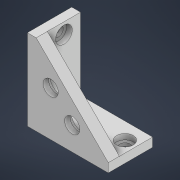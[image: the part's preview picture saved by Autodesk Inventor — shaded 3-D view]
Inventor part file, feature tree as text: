
AUTODESK INVENTOR PART (.ipt)
format: ipt  version: 2022 (Build 260153000, 153)  size: 154,112 bytes
history: native  units: mm
features: sketch x6, extrude x3, hole x3
ambient origin geometry x8: Origin, YZ Plane, XZ Plane, XY Plane, X Axis, Y Axis, Z Axis, Center Point
bodies: Volumenkörper1 (feature_tree)
feature tree (12):
  extrude  "Extrusion1"  Depth=26.0mm
  hole  "Bohrung1"  [1 undecoded]
  extrude  "Extrusion2"  Depth=13.0mm
  extrude  "Extrusion3"  Depth=9.0mm
  hole  "Bohrung2"  [1 undecoded]
  hole  "Bohrung3"  [1 undecoded]
  sketch  "Skizze1"  dims[d0=26.0mm d1=26.0mm]
  sketch  "Skizze2"  dims[d2=4.0mm d3=0.0mm]
  sketch  "Skizze3"  dims[d4=5.5mm d5=6.0mm d6=4.0mm d7=2.0mm d8=90.0deg d9=8.0mm d10=20.594885mm d11=5.5mm]
  sketch  "Skizze4"  dims[d12=5.5mm d14=13.0mm]
  sketch  "Skizze5"  dims[d15=13.0mm d16=9.0mm]
  sketch  "Skizze6"  dims[d17=9.0mm d18=2.0mm d19=0.0mm d20=3.2mm d21=3.2mm d22=16.0mm d23=0.0mm d24=3.5mm d25=6.0mm d26=6.0mm d27=2.0mm d28=90.0deg d29=8.0mm d30=20.594885mm d31=4.0mm d32=6.0mm d33=3.5mm d34=6.0mm d35=6.0mm d36=2.0mm d37=90.0deg d38=8.0mm d39=20.594885mm d40=6.0mm d41=4.0mm]
note: 3 required parameter values undecoded (feature->parameter linkage not recoverable at this tier; creation-order binding heuristic only, values carry confidence <= 0.55)
